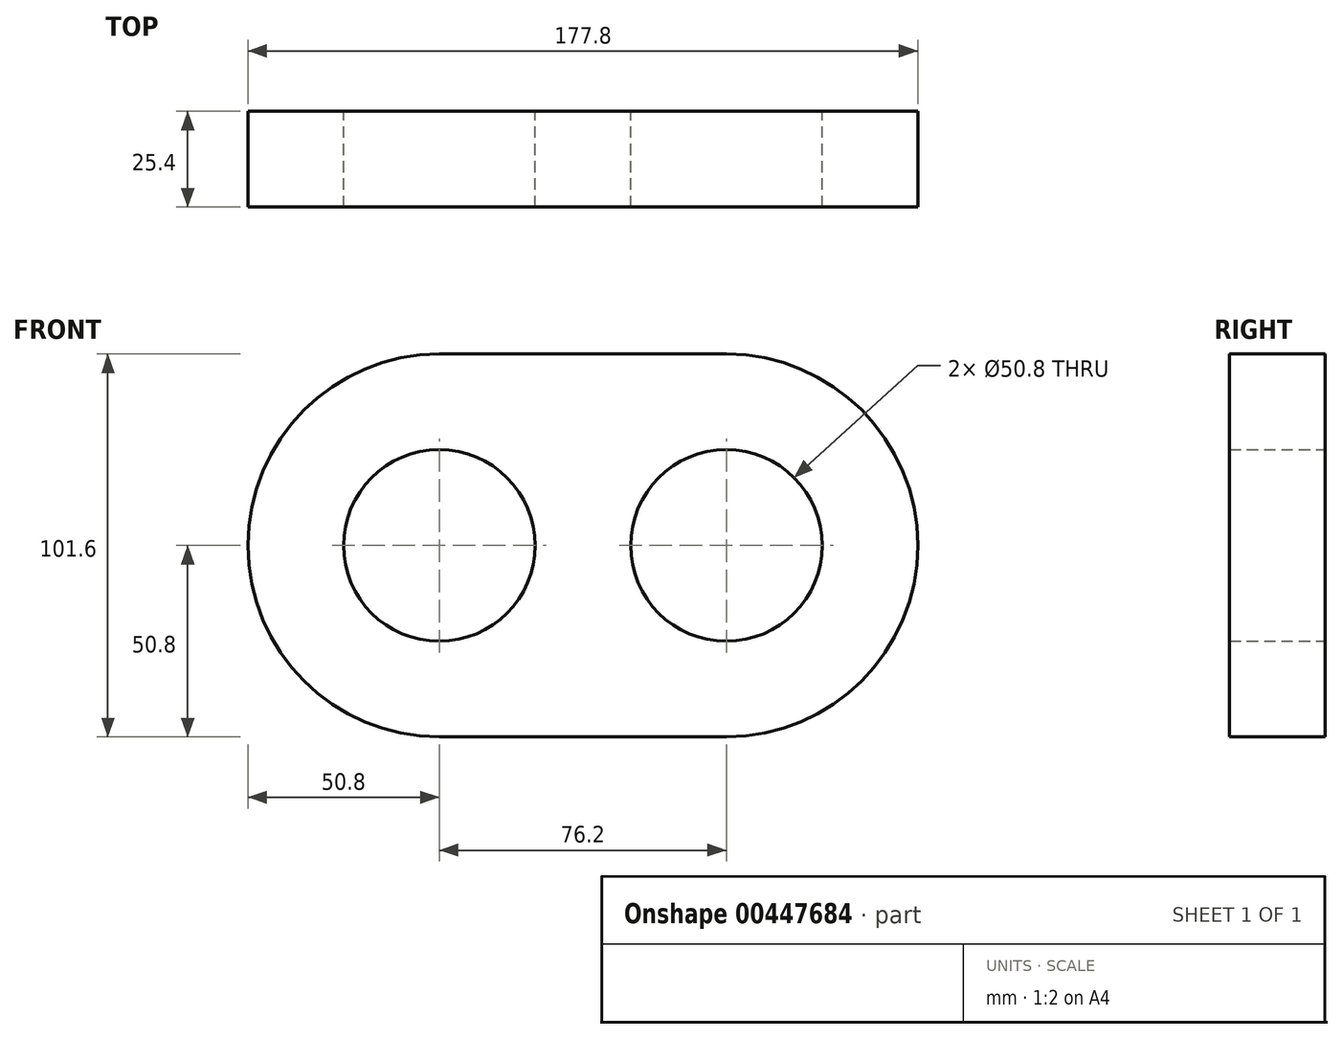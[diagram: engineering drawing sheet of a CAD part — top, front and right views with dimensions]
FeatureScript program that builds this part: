
annotation { "Feature Type Name" : "Feature", "Feature Type Description" : "" }
export const myFeature = defineFeature(function(context is Context, id is Id, definition is map)
    precondition{}
    {
        {
            var Q0;
            Q0=qCreatedBy(makeId("Front.planeOp"),FACE);
            var sketch = newSketch(context, id + "F0", { "sketchPlane" : qUnion([Q0])});
            skCircle(sketch, "E0", {"center": v(0, 0) * mm, "radius": 50.8 * mm});
            skLineSegment(sketch, "E1.bottom", {"start": v(0, 50.8) * mm, "end": v(127, 50.8) * mm});
            skLineSegment(sketch, "E1.top", {"start": v(0, -50.8) * mm, "end": v(127, -50.8) * mm});
            skLineSegment(sketch, "E1.left", {"start": v(0, 50.8) * mm, "end": v(0, -50.8) * mm});
            skLineSegment(sketch, "E1.right", {"start": v(127, 50.8) * mm, "end": v(127, -50.8) * mm});
            skSolve(sketch);
        }
        {
            var Q0;
            Q0 = qSketchRegion(id + "F0", true);
            extrude(context, id + "F1", {"entities" : qUnion([Q0]), "depth" : 25.4 * mm});
        }
        {
            var Q0;
            Q0=makeQuery(id+"F1.opExtrude","SWEPT_EDGE",EDGE,{"disambiguationData":[OSD([sQuery(id+"F0.wireOp",EDGE,"E1.bottom"),sQuery(id+"F0.wireOp",EDGE,"E1.right")])]});
            var Q1;
            Q1=makeQuery(id+"F1.opExtrude","SWEPT_EDGE",EDGE,{"disambiguationData":[OSD([sQuery(id+"F0.wireOp",EDGE,"E1.top"),sQuery(id+"F0.wireOp",EDGE,"E1.right")])]});
            fillet(context, id + "F2", {"entities" : qUnion([Q0, Q1]), "radius" : 50.8 * mm, "tangentPropagation" : true, "allowEdgeOverflow" : false});
        }
        {
            var Q0;
            Q0=qCreatedBy(makeId("Front.planeOp"),FACE);
            var sketch = newSketch(context, id + "F3", { "sketchPlane" : qUnion([Q0])});
            skCircle(sketch, "E2", {"center": v(0, 0) * mm, "radius": 25.4 * mm});
            skSolve(sketch);
        }
        {
            var Q0;
            Q0 = qSketchRegion(id + "F3", true);
            extrude(context, id + "F4", {"entities" : qUnion([Q0]), "operationType" : NewBodyOperationType.REMOVE, "depth" : 25.4 * mm});
        }
        {
            var Q0;
            Q0=qCreatedBy(makeId("Right.planeOp"),FACE);
            cPlane(context, id + "F5", {"entities" : qUnion([Q0]), "cplaneType" : CPlaneType.OFFSET, "offset" : 38.1 * mm, "width" : 152.4 * mm, "height" : 152.4 * mm});
        }
        {
            var Q0;
            Q0=makeQuery(id+"F4.boolean.opBoolean","COPY",FACE,{"derivedFrom":makeQuery(id+"F4.opExtrude","SWEPT_FACE",FACE,{"disambiguationData":[OSD([sQuery(id+"F3.wireOp",EDGE,"E2")])]})});
            var Q1;
            Q1=qCreatedBy(id+"F5.planeOp",FACE);
            mirror(context, id + "F6", {"patternType" : MirrorType.FACE, "faces" : qUnion([Q0]), "mirrorPlane" : qUnion([Q1])});
        }
    });
